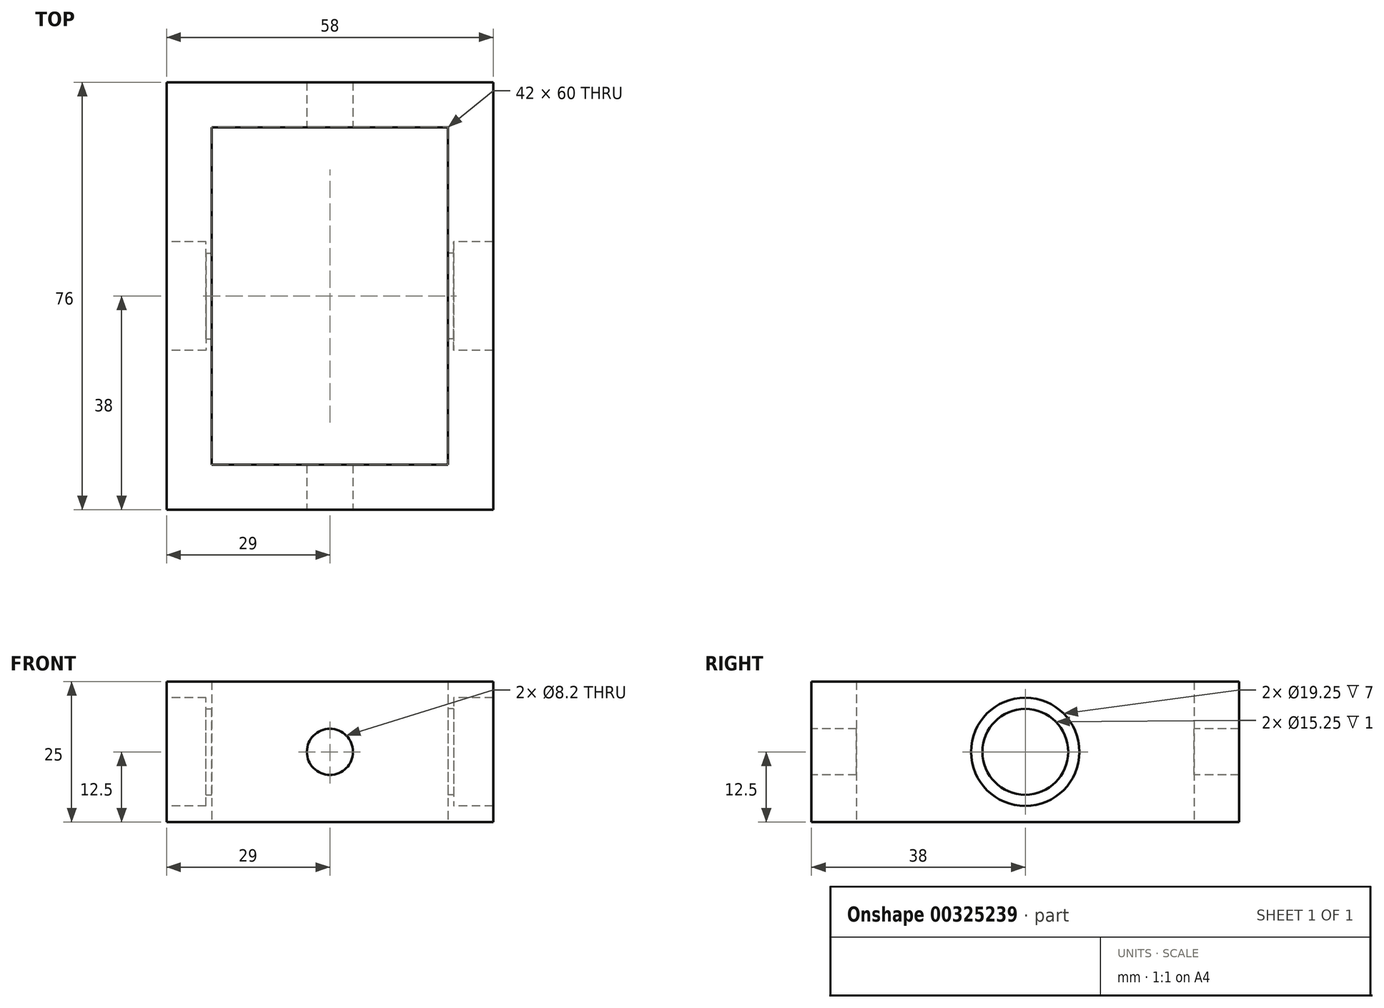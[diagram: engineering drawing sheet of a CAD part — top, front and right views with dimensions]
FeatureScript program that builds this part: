
annotation { "Feature Type Name" : "Feature", "Feature Type Description" : "" }
export const myFeature = defineFeature(function(context is Context, id is Id, definition is map)
    precondition{}
    {
        {
            var Q0;
            Q0=qCreatedBy(makeId("Top.planeOp"),FACE);
            var sketch = newSketch(context, id + "F0", { "sketchPlane" : qUnion([Q0])});
            skLineSegment(sketch, "E0.bottom", {"start": v(21, -30) * mm, "end": v(-21, -30) * mm});
            skLineSegment(sketch, "E0.top", {"start": v(21, 30) * mm, "end": v(-21, 30) * mm});
            skLineSegment(sketch, "E0.left", {"start": v(21, -30) * mm, "end": v(21, 30) * mm});
            skLineSegment(sketch, "E0.right", {"start": v(-21, -30) * mm, "end": v(-21, 30) * mm});
            skPoint(sketch, "E0.middle", {"position": v(0, 0) * mm});
            skLineSegment(sketch, "E1.0", {"start": v(29, 38) * mm, "end": v(-29, 38) * mm});
            skLineSegment(sketch, "E1.1", {"start": v(29, -38) * mm, "end": v(29, 38) * mm});
            skLineSegment(sketch, "E1.2", {"start": v(29, -38) * mm, "end": v(-29, -38) * mm});
            skLineSegment(sketch, "E1.3", {"start": v(-29, -38) * mm, "end": v(-29, 38) * mm});
            skSolve(sketch);
        }
        {
            var Q0;
            Q0 = qSketchRegion(id + "F0", true);
            extrude(context, id + "F1", {"entities" : qUnion([Q0]), "depth" : 25 * mm});
        }
        {
            var Q0;
            Q0=makeQuery(id+"F1.opExtrude","SWEPT_FACE",FACE,{"disambiguationData":[OSD([sQuery(id+"F0.wireOp",EDGE,"E1.3")])]});
            var sketch = newSketch(context, id + "F2", { "sketchPlane" : qUnion([Q0])});
            skCircle(sketch, "E2", {"center": v(0, 12.5) * mm, "radius": 9.62 * mm});
            skPoint(sketch, "E2.centerSnap0", {"position": v(38, 12.5) * mm});
            skPoint(sketch, "E2.centerSnap1", {"position": v(0, 25) * mm});
            skSolve(sketch);
        }
        {
            var Q0;
            Q0 = qSketchRegion(id + "F2", true);
            var Q1;
            Q1=makeQuery(id+"F1.opExtrude","SWEPT_FACE",FACE,{"disambiguationData":[OSD([sQuery(id+"F0.wireOp",EDGE,"E1.1")])]});
            extrude(context, id + "F3", {"entities" : qUnion([Q0]), "operationType" : NewBodyOperationType.REMOVE, "endBound" : BoundingType.UP_TO_SURFACE, "oppositeDirection" : true, "endBoundEntityFace" : qUnion([Q1]), "depth" : 25 * mm});
        }
        {
            var Q0;
            Q0=makeQuery(id+"F1.opExtrude","SWEPT_FACE",FACE,{"disambiguationData":[OSD([sQuery(id+"F0.wireOp",EDGE,"E1.2")])]});
            var sketch = newSketch(context, id + "F4", { "sketchPlane" : qUnion([Q0])});
            skCircle(sketch, "E3", {"center": v(0, 12.5) * mm, "radius": 4.1 * mm});
            skPoint(sketch, "E3.centerSnap0", {"position": v(29, 12.5) * mm});
            skPoint(sketch, "E3.centerSnap1", {"position": v(0, 25) * mm});
            skSolve(sketch);
        }
        {
            var Q0;
            Q0 = qSketchRegion(id + "F4", true);
            var Q1;
            Q1=makeQuery(id+"F1.opExtrude","SWEPT_FACE",FACE,{"disambiguationData":[OSD([sQuery(id+"F0.wireOp",EDGE,"E1.0")])]});
            extrude(context, id + "F5", {"entities" : qUnion([Q0]), "operationType" : NewBodyOperationType.REMOVE, "endBound" : BoundingType.UP_TO_SURFACE, "oppositeDirection" : true, "endBoundEntityFace" : qUnion([Q1]), "depth" : 25 * mm});
        }
        {
            var Q0;
            Q0=makeQuery(id+"F1.opExtrude","SWEPT_FACE",FACE,{"disambiguationData":[OSD([sQuery(id+"F0.wireOp",EDGE,"E0.right")])]});
            var sketch = newSketch(context, id + "F6", { "sketchPlane" : qUnion([Q0])});
            skCircle(sketch, "E4.0", {"center": v(0, 12.5) * mm, "radius": 7.62 * mm});
            skCircle(sketch, "E5.0", {"center": v(0, 12.5) * mm, "radius": 9.62 * mm});
            skSolve(sketch);
        }
        {
            var Q0;
            Q0 = qSketchRegion(id + "F6", true);
            extrude(context, id + "F7", {"entities" : qUnion([Q0]), "operationType" : NewBodyOperationType.ADD, "oppositeDirection" : true, "depth" : 1 * mm});
        }
        {
            var Q0;
            Q0=makeQuery(id+"F1.opExtrude","SWEPT_FACE",FACE,{"disambiguationData":[OSD([sQuery(id+"F0.wireOp",EDGE,"E0.left")])]});
            var sketch = newSketch(context, id + "F8", { "sketchPlane" : qUnion([Q0])});
            skCircle(sketch, "E6.0", {"center": v(0, 12.5) * mm, "radius": 7.62 * mm});
            skCircle(sketch, "E7.0", {"center": v(0, 12.5) * mm, "radius": 9.62 * mm});
            skSolve(sketch);
        }
        {
            var Q0;
            Q0 = qSketchRegion(id + "F8", true);
            extrude(context, id + "F9", {"entities" : qUnion([Q0]), "operationType" : NewBodyOperationType.ADD, "oppositeDirection" : true, "depth" : 1 * mm});
        }
    });
